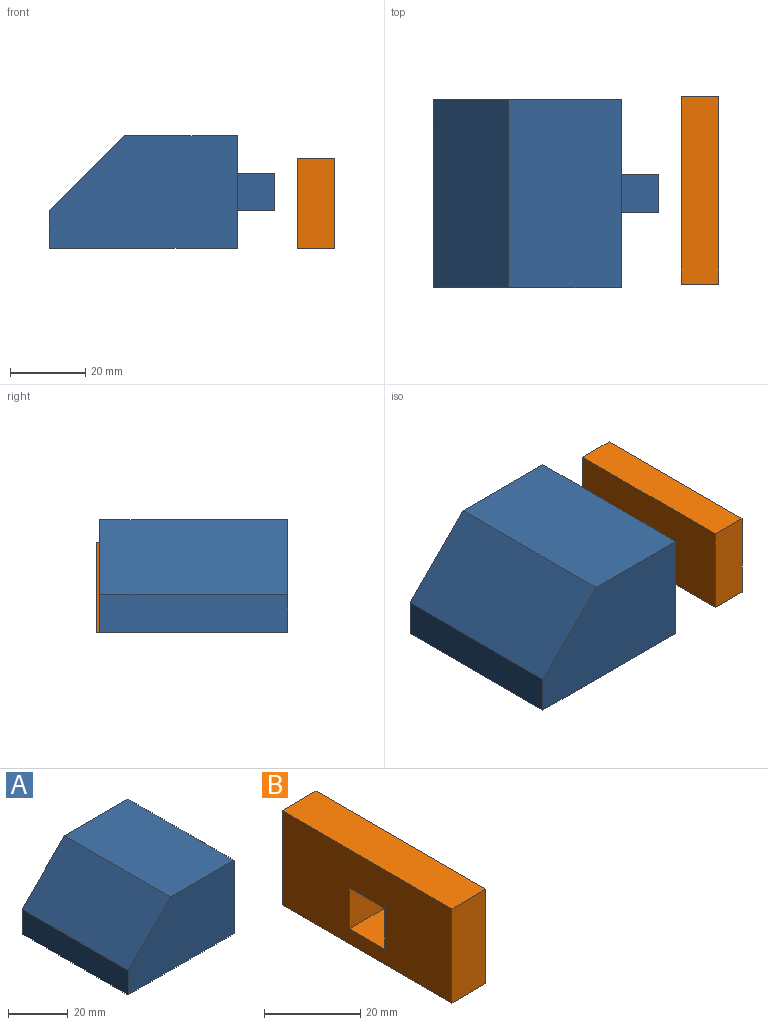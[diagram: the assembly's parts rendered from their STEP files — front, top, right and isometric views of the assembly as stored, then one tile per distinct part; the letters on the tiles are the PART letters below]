
ASSEMBLY  parts=2 mates=1
PART A: 12 faces, bbox 60x50x30 mm
  f0: plane 50x50mm, normal (0,0,-1), area 2500mm2, adj f1,f3,f9,f10
  f1: plane 50x30mm, normal (1,0,0), area 1400mm2, adj f0,f2,f4,f5,f6,f7,f9,f10
  f2: plane 50x30mm, normal (0,0,1), area 1500mm2, adj f1,f9,f10,f11
  f3: plane 50x10mm, normal (-1,0,0), area 500mm2, adj f0,f9,f10,f11
  f4: plane 10x10mm, normal (0,0,-1), area 100mm2, adj f1,f5,f7,f8
  f5: plane 10x10mm, normal (0,1,0), area 100mm2, adj f1,f4,f6,f8
  f6: plane 10x10mm, normal (0,0,1), area 100mm2, adj f1,f5,f7,f8
  f7: plane 10x10mm, normal (0,-1,0), area 100mm2, adj f1,f4,f6,f8
  f8: plane 10x10mm, normal (1,0,0), area 100mm2, adj f4,f5,f6,f7
  f9: plane 50x30mm, normal (0,-1,0), area 1300mm2, adj f0,f1,f2,f3,f11
  f10: plane 50x30mm, normal (0,1,0), area 1300mm2, adj f0,f1,f2,f3,f11
  f11: plane 50x20mm, normal (-0.71,0,0.71), area 1414.2mm2, adj f2,f3,f9,f10
PART B: 10 faces, bbox 10x50x24 mm
  f0: plane 50x10mm, normal (0,0,-1), area 500mm2, adj f6,f7,f8,f9
  f1: plane 50x10mm, normal (0,0,1), area 500mm2, adj f6,f7,f8,f9
  f2: plane 10.4x10mm, normal (0,-1,0), area 104mm2, adj f3,f5,f6,f7
  f3: plane 10.4x10mm, normal (0,0,1), area 104mm2, adj f2,f4,f6,f7
  f4: plane 10.4x10mm, normal (0,1,0), area 104mm2, adj f3,f5,f6,f7
  f5: plane 10.4x10mm, normal (0,0,-1), area 104mm2, adj f2,f4,f6,f7
  f6: plane 50x24mm, normal (1,0,0), area 1091.8mm2, adj f0,f1,f2,f3,f4,f5,f8,f9
  f7: plane 50x24mm, normal (-1,0,0), area 1091.8mm2, adj f0,f1,f2,f3,f4,f5,f8,f9
  f8: plane 24x10mm, normal (0,-1,0), area 240mm2, adj f0,f1,f6,f7
  f9: plane 24x10mm, normal (0,1,0), area 240mm2, adj f0,f1,f6,f7
PLACE A t=(-20.98,3.73,-3.95)mm
PLACE B t=(-30.09,4.69,-9.95)mm
MATE planar A.f0 <-> B.f0  axis (0,0,-1) through (-45.98,-16.27,-3.95)mm
